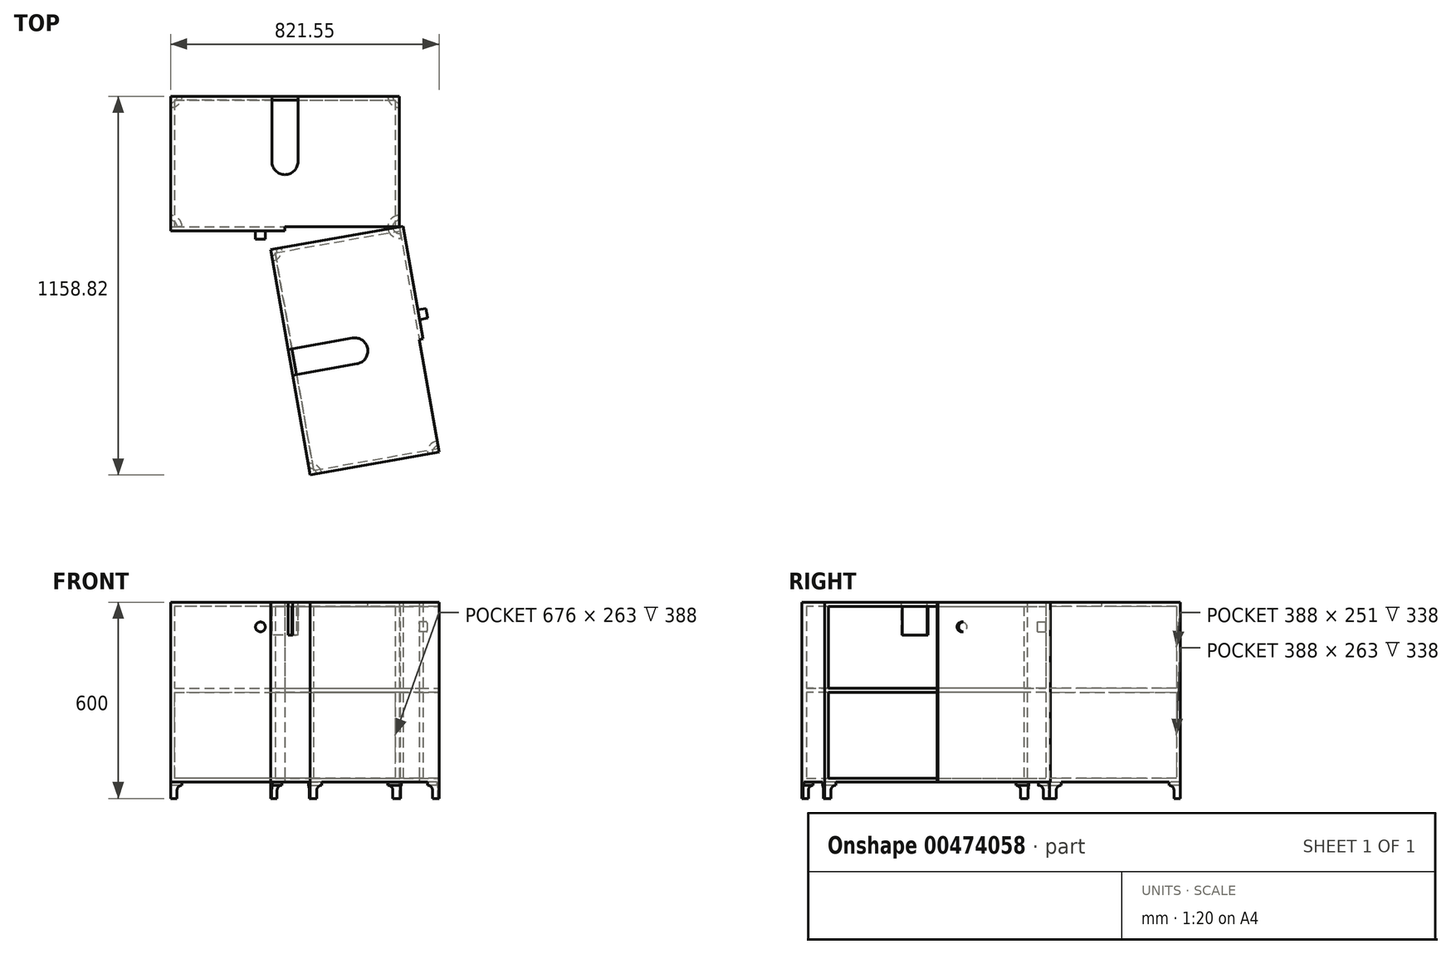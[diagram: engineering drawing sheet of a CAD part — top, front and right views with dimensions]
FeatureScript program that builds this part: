
annotation { "Feature Type Name" : "Feature", "Feature Type Description" : "" }
export const myFeature = defineFeature(function(context is Context, id is Id, definition is map)
    precondition{}
    {
        {
            var Q0;
            Q0=qCreatedBy(makeId("Top.planeOp"),FACE);
            var sketch = newSketch(context, id + "F0", { "sketchPlane" : qUnion([Q0])});
            skLineSegment(sketch, "E0.right", {"start": v(-350, 200) * mm, "end": v(-350, -200) * mm});
            skPoint(sketch, "E0.middle", {"position": v(0, 0) * mm});
            skLineSegment(sketch, "E1", {"start": v(0, -200) * mm, "end": v(0, 200) * mm});
            skLineSegment(sketch, "E2", {"start": v(0, 200) * mm, "end": v(-350, 200) * mm});
            skLineSegment(sketch, "E3", {"start": v(0, -200) * mm, "end": v(-350, -200) * mm});
            skSolve(sketch);
        }
        {
            var Q0;
            Q0=makeQuery(id+"F0.imprint","IMPRINT",FACE,{"disambiguationData":[TD([[makeQuery(id+"F0.imprint","IMPRINT",EDGE,{"derivedFrom":sQuery(id+"F0.wireOp",EDGE,"E0.bottom")}),1.0]])]});
            var Q1;
            Q1=makeQuery(id+"F0.imprint","IMPRINT",FACE,{"disambiguationData":[TD([[makeQuery(id+"F0.imprint","IMPRINT",EDGE,{"derivedFrom":sQuery(id+"F0.wireOp",EDGE,"E0.right")}),1.0]])]});
            extrude(context, id + "F1", {"entities" : qUnion([Q0, Q1]), "depth" : 550 * mm});
        }
        {
            var Q0;
            Q0=makeQuery(id+"F1.opExtrude","SWEPT_FACE",FACE,{"disambiguationData":[OSD([sQuery(id+"F0.wireOp",EDGE,"E0.top")])]});
            var Q1;
            Q1=makeQuery(id+"F1.opExtrude","SWEPT_FACE",FACE,{"disambiguationData":[OSD([sQuery(id+"F0.wireOp",EDGE,"E3")])]});
            var Q2;
            Q2=makeQuery(id+"F1.opExtrude","SWEPT_FACE",FACE,{"disambiguationData":[OSD([sQuery(id+"F0.wireOp",EDGE,"E1")])]});
            shell(context, id + "F2", {"entities" : qUnion([Q0, Q1, Q2]), "thickness" : 12 * mm});
        }
        {
            var Q0;
            Q0=makeQuery(id+"F1.opExtrude","SWEPT_FACE",FACE,{"disambiguationData":[OSD([sQuery(id+"F0.wireOp",EDGE,"E0.right")])]});
            var sketch = newSketch(context, id + "F3", { "sketchPlane" : qUnion([Q0])});
            skLineSegment(sketch, "E4", {"start": v(-200, 0) * mm, "end": v(-200, -50) * mm});
            skLineSegment(sketch, "E5", {"start": v(-200, -50) * mm, "end": v(-180, -50) * mm});
            skLineSegment(sketch, "E6", {"start": v(-180, -50) * mm, "end": v(-180, -25) * mm});
            skLineSegment(sketch, "E7", {"start": v(-165, -10) * mm, "end": v(-165, 0) * mm});
            skLineSegment(sketch, "E8", {"start": v(-165, 0) * mm, "end": v(-200, 0) * mm});
            skArc(sketch, "E9", {"start": v(-165, -10) * mm, "mid": v(-175.6, -14.4) * mm, "end": v(-180, -25) * mm});
            skLineSegment(sketch, "E10", {"start": v(-165, -10) * mm, "end": v(-155, -10) * mm});
            skSolve(sketch);
        }
        {
            var Q0;
            Q0=makeQuery(id+"F3.imprint","IMPRINT",FACE,{"disambiguationData":[TD([[makeQuery(id+"F3.imprint","IMPRINT",EDGE,{"derivedFrom":sQuery(id+"F3.wireOp",EDGE,"E4")}),1.0]])]});
            var Q1;
            Q1=sQuery(id+"F3.wireOp",EDGE,"E4");
            revolve(context, id + "F4", {"entities" : qUnion([Q0]), "axis" : qUnion([Q1]), "revolveType" : RevolveType.ONE_DIRECTION, "oppositeDirection" : true, "angle" : 90 * degree});
        }
        {
            var Q0;
            Q0=makeQuery(id+"F4.opRevolve","SWEPT_BODY",BODY,{"disambiguationData":[OSD([sQuery(id+"F3.wireOp",EDGE,"E4"),sQuery(id+"F3.wireOp",EDGE,"E5"),sQuery(id+"F3.wireOp",EDGE,"E6"),sQuery(id+"F3.wireOp",EDGE,"E7"),sQuery(id+"F3.wireOp",EDGE,"E8"),sQuery(id+"F3.wireOp",EDGE,"E9")])]});
            var Q1;
            Q1=qCreatedBy(makeId("Front.planeOp"),FACE);
            mirror(context, id + "F5", {"operationType" : NewBodyOperationType.ADD, "entities" : qUnion([Q0]), "mirrorPlane" : qUnion([Q1])});
        }
        {
            var Q0;
            Q0=qCreatedBy(makeId("Right.planeOp"),FACE);
            var sketch = newSketch(context, id + "F6", { "sketchPlane" : qUnion([Q0])});
            skLineSegment(sketch, "E11.0", {"start": v(188, 538) * mm, "end": v(188, 12) * mm, "construction": true});
            skLineSegment(sketch, "E12", {"start": v(188, 275) * mm, "end": v(-200, 275) * mm});
            skLineSegment(sketch, "E13", {"start": v(-200, 275) * mm, "end": v(-200, 287) * mm});
            skLineSegment(sketch, "E14", {"start": v(-200, 287) * mm, "end": v(188, 287) * mm});
            skLineSegment(sketch, "E15.0", {"start": v(-200, 538) * mm, "end": v(-200, 12) * mm, "construction": true});
            skLineSegment(sketch, "E16", {"start": v(188, 287) * mm, "end": v(188, 275) * mm});
            skSolve(sketch);
        }
        {
            var Q0;
            Q0 = qSketchRegion(id + "F6", true);
            extrude(context, id + "F7", {"entities" : qUnion([Q0]), "operationType" : NewBodyOperationType.ADD, "endBound" : BoundingType.UP_TO_NEXT, "oppositeDirection" : true, "depth" : 25 * mm});
        }
        {
            var Q0;
            Q0=makeQuery(id+"F7.boolean.opBoolean","MERGE",FACE,{"derivedFrom":[makeQuery(id+"F5.boolean.opBoolean","MERGE",FACE,{"derivedFrom":[makeQuery(id+"F1.opExtrude","SWEPT_FACE",FACE,{"disambiguationData":[OSD([sQuery(id+"F0.wireOp",EDGE,"E3")])]}),makeQuery(id+"F5.opPattern","COPY",FACE,{"derivedFrom":makeQuery(id+"F4.opRevolve","CAP_FACE",FACE,{"disambiguationData":[OSD([sQuery(id+"F3.wireOp",EDGE,"E4"),sQuery(id+"F3.wireOp",EDGE,"E5"),sQuery(id+"F3.wireOp",EDGE,"E6"),sQuery(id+"F3.wireOp",EDGE,"E7"),sQuery(id+"F3.wireOp",EDGE,"E8"),sQuery(id+"F3.wireOp",EDGE,"E9")])],"isStart":false}),"instanceName":"1"})]}),makeQuery(id+"F7.opExtrude","SWEPT_FACE",FACE,{"disambiguationData":[OSD([sQuery(id+"F6.wireOp",EDGE,"E13")])]})]});
            var sketch = newSketch(context, id + "F8", { "sketchPlane" : qUnion([Q0])});
            skLineSegment(sketch, "E17.bottom", {"start": v(-350, 550) * mm, "end": v(0, 550) * mm});
            skLineSegment(sketch, "E17.top", {"start": v(-350, 0) * mm, "end": v(0, 0) * mm});
            skLineSegment(sketch, "E17.left", {"start": v(-350, 550) * mm, "end": v(-350, 0) * mm});
            skLineSegment(sketch, "E17.right", {"start": v(0, 550) * mm, "end": v(0, 0) * mm});
            skSolve(sketch);
        }
        {
            var Q0;
            Q0 = qSketchRegion(id + "F8", true);
            extrude(context, id + "F9", {"entities" : qUnion([Q0]), "depth" : 12 * mm});
        }
        {
            var Q0;
            Q0=makeQuery(id+"F9.opExtrude","CAP_FACE",FACE,{"disambiguationData":[OSD([sQuery(id+"F8.wireOp",EDGE,"E17.bottom"),sQuery(id+"F8.wireOp",EDGE,"E17.top"),sQuery(id+"F8.wireOp",EDGE,"E17.left"),sQuery(id+"F8.wireOp",EDGE,"E17.right")])],"isStart":false});
            var sketch = newSketch(context, id + "F10", { "sketchPlane" : qUnion([Q0])});
            skCircle(sketch, "E18", {"center": v(-75, 475) * mm, "radius": 15 * mm});
            skSolve(sketch);
        }
        {
            var Q0;
            Q0 = qSketchRegion(id + "F10", true);
            extrude(context, id + "F11", {"entities" : qUnion([Q0]), "operationType" : NewBodyOperationType.ADD, "depth" : 25 * mm});
        }
        {
            var Q0;
            Q0=makeQuery(id+"F1.opExtrude","CAP_FACE",FACE,{"disambiguationData":[OSD([sQuery(id+"F0.wireOp",EDGE,"E0.right"),sQuery(id+"F0.wireOp",EDGE,"E1"),sQuery(id+"F0.wireOp",EDGE,"E2"),sQuery(id+"F0.wireOp",EDGE,"E3")])],"isStart":false});
            var sketch = newSketch(context, id + "F12", { "sketchPlane" : qUnion([Q0])});
            skLineSegment(sketch, "E19", {"start": v(-40, 200) * mm, "end": v(-40, 0) * mm});
            skArc(sketch, "E20", {"start": v(-40, 0) * mm, "mid": v(-28.28, -28.28) * mm, "end": v(0, -40) * mm});
            skLineSegment(sketch, "E21", {"start": v(0, -40) * mm, "end": v(200, -40) * mm, "construction": true});
            skLineSegment(sketch, "E22", {"start": v(0, -40) * mm, "end": v(0, 200) * mm});
            skLineSegment(sketch, "E23", {"start": v(0, 200) * mm, "end": v(-40, 200) * mm});
            skSolve(sketch);
        }
        {
            var Q0;
            Q0 = qSketchRegion(id + "F12", true);
            extrude(context, id + "F13", {"entities" : qUnion([Q0]), "operationType" : NewBodyOperationType.REMOVE, "oppositeDirection" : true, "depth" : 100 * mm});
        }
        {
            var Q0;
            Q0=makeQuery(id+"F1.opExtrude","SWEPT_BODY",BODY,{"disambiguationData":[OSD([sQuery(id+"F0.wireOp",EDGE,"E0.right"),sQuery(id+"F0.wireOp",EDGE,"E1"),sQuery(id+"F0.wireOp",EDGE,"E2"),sQuery(id+"F0.wireOp",EDGE,"E3")])]});
            var Q1;
            Q1=qCreatedBy(makeId("Right.planeOp"),FACE);
            mirror(context, id + "F14", {"operationType" : NewBodyOperationType.ADD, "entities" : qUnion([Q0]), "mirrorPlane" : qUnion([Q1])});
        }
        {
            var Q0;
            Q0=makeQuery(id+"F9.opExtrude","SWEPT_BODY",BODY,{"disambiguationData":[OSD([sQuery(id+"F8.wireOp",EDGE,"E17.bottom"),sQuery(id+"F8.wireOp",EDGE,"E17.top"),sQuery(id+"F8.wireOp",EDGE,"E17.left"),sQuery(id+"F8.wireOp",EDGE,"E17.right")])]});
            var Q1;
            Q1=qCreatedBy(makeId("Right.planeOp"),FACE);
            mirror(context, id + "F15", {"entities" : qUnion([Q0]), "mirrorPlane" : qUnion([Q1])});
        }
        {
            var Q0;
            Q0=makeQuery(id+"F15.opPattern","COPY",BODY,{"derivedFrom":makeQuery(id+"F9.opExtrude","SWEPT_BODY",BODY,{"disambiguationData":[OSD([sQuery(id+"F8.wireOp",EDGE,"E17.bottom"),sQuery(id+"F8.wireOp",EDGE,"E17.top"),sQuery(id+"F8.wireOp",EDGE,"E17.left"),sQuery(id+"F8.wireOp",EDGE,"E17.right")])]}),"instanceName":"1"});
            var Q1;
            Q1=makeQuery(id+"F14.opPattern","COPY",EDGE,{"derivedFrom":makeQuery(id+"F5.boolean.opBoolean","MERGE",EDGE,{"derivedFrom":[makeQuery(id+"F1.opExtrude","SWEPT_EDGE",EDGE,{"disambiguationData":[OSD([sQuery(id+"F0.wireOp",EDGE,"E0.right"),sQuery(id+"F0.wireOp",EDGE,"E3")])]}),makeQuery(id+"F5.opPattern","COPY",EDGE,{"derivedFrom":makeQuery(id+"F4.opRevolve","CAP_EDGE",EDGE,{"disambiguationData":[OSD([sQuery(id+"F3.wireOp",EDGE,"E4")])],"isStart":true}),"instanceName":"1"})]}),"instanceName":"1"});
            transform(context, id + "F16", {"entities" : qUnion([Q0]), "transformType" : TransformType.ROTATION, "transformAxis" : qUnion([Q1]), "angle" : 100 * degree, "oppositeDirection" : true, "makeCopy" : false});
        }
    });
